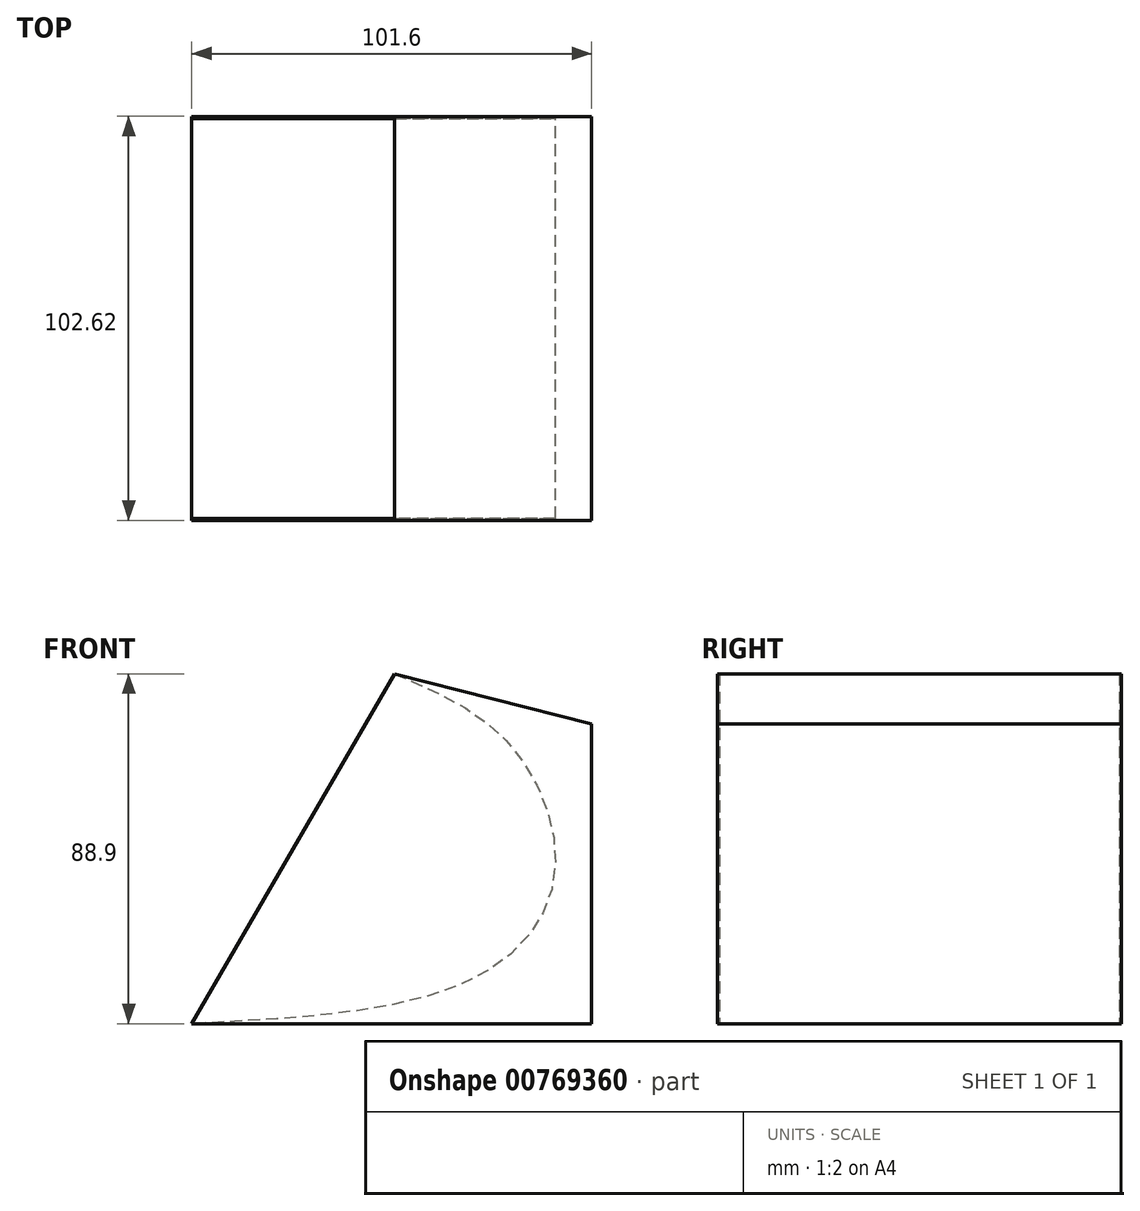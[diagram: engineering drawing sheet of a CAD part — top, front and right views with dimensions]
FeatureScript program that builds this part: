
annotation { "Feature Type Name" : "Feature", "Feature Type Description" : "" }
export const myFeature = defineFeature(function(context is Context, id is Id, definition is map)
    precondition{}
    {
        {
            var Q0;
            Q0=qCreatedBy(makeId("Front.planeOp"),FACE);
            var sketch = newSketch(context, id + "F0", { "sketchPlane" : qUnion([Q0])});
            skLineSegment(sketch, "E0", {"start": v(-0.42, -35.32) * mm, "end": v(-0.42, 40.88) * mm});
            skLineSegment(sketch, "E1", {"start": v(-0.42, -35.32) * mm, "end": v(-102.02, -35.32) * mm});
            skLineSegment(sketch, "E2", {"start": v(-50.52, 53.58) * mm, "end": v(-0.42, 40.88) * mm});
            skFitSpline(sketch, "E3", {"points": [v(-50.52, 53.58) * mm, v(-21.56, 35.95) * mm, v(-9.83, 2.85) * mm, v(-30.14, -23.72) * mm, v(-102.02, -35.32) * mm], "startDerivative": vector(142.05, -60.57) * mm, "endDerivative": vector(-249.6, -12.42) * mm});
            skSolve(sketch);
        }
        {
            var Q0;
            Q0 = qSketchRegion(id + "F0", true);
            extrude(context, id + "F1", {"entities" : qUnion([Q0]), "depth" : 50.8 * mm, "offsetDistance" : 25.4 * mm});
        }
        {
            var Q0;
            Q0=makeQuery(id+"F1.opExtrude","CAP_FACE",FACE,{"disambiguationData":[OSD([sQuery(id+"F0.wireOp",EDGE,"E0"),sQuery(id+"F0.wireOp",EDGE,"E1"),sQuery(id+"F0.wireOp",EDGE,"E2"),sQuery(id+"F0.wireOp",EDGE,"E3")])],"isStart":false});
            var sketch = newSketch(context, id + "F2", { "sketchPlane" : qUnion([Q0])});
            skLineSegment(sketch, "E4", {"start": v(-50.52, 53.58) * mm, "end": v(-102.02, -35.32) * mm});
            skLineSegment(sketch, "E5", {"start": v(-50.52, 53.58) * mm, "end": v(-0.42, 40.88) * mm});
            skLineSegment(sketch, "E6", {"start": v(-0.42, 40.88) * mm, "end": v(-0.42, -35.32) * mm});
            skLineSegment(sketch, "E7", {"start": v(-0.42, -35.32) * mm, "end": v(-102.02, -35.32) * mm});
            skSolve(sketch);
        }
        {
            var Q0;
            Q0 = qSketchRegion(id + "F2", true);
            extrude(context, id + "F3", {"entities" : qUnion([Q0]), "operationType" : NewBodyOperationType.ADD, "depth" : 0.5 * mm, "offsetDistance" : 25.4 * mm});
        }
        {
            var Q0;
            Q0=makeQuery(id+"F1.opExtrude","SWEPT_BODY",BODY,{"disambiguationData":[OSD([sQuery(id+"F0.wireOp",EDGE,"E0"),sQuery(id+"F0.wireOp",EDGE,"E1"),sQuery(id+"F0.wireOp",EDGE,"E2"),sQuery(id+"F0.wireOp",EDGE,"E3")])]});
            var Q1;
            Q1=qCreatedBy(makeId("Front.planeOp"),FACE);
            mirror(context, id + "F4", {"operationType" : NewBodyOperationType.ADD, "entities" : qUnion([Q0]), "mirrorPlane" : qUnion([Q1])});
        }
    });
